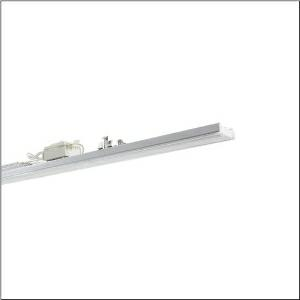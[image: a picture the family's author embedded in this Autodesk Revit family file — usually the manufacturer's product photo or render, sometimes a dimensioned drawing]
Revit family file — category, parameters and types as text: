
# Revit family: licross_11_recessed_mo_51te12dn4axg3s
name_source: partatom
category: Lighting Fixtures
units: mm (PartAtom-declared; Revit-internal decimal feet)

## family parameters
Cut with Voids When Loaded = No
Host = Face
Light Source = No
Part Type = Normal
Room Calculation Point = No
Round Connector Dimension = Use Diameter
Shared = No

## types (1)
- --- (1 x LED, 1010 lm, 6.7 W, 4000K)
    Apparent Load = 7 VA
    CIE Flux Codes = 67 92 99 100 100
    Color Rendering = 80
    Color Temperature = 4000K
    Default Elevation = 1800 mm
    Description = Licross 11 Recessed MO, luminaire insert, of sheet steel, galvanised, coil coated, white, length: 1.500mm, width: 66mm, height: 67mm, LED rated luminous flux: 10.240lm, light colour: 840, SDCM (Standard Deviation of Colour Matching)MacAdam ≤ 2 SDCM (initial), control gear: DALI 2 (for two DALI lines), with plug, 6-pole, with phase selection, for trunking rail, 14-core, mains connection: 220..240V, AC, 50/60Hz, rated input power: 61W, for trunking rail, 14-core, internal wiring halogen-free, for emergency light function, converter,control gear: single battery element, battery: LiFePO4, 9Ah, primary optical cover: cover, of PMMA, light emission: direct distribution, primary light characteristic: symmetric, protection rating (complete): IP54, insulation class (complete): insulation class I (protective earthing), certification: CE, UKCA, protection symbol: D if used in an environment with non-conductive dust loads with corresponding accessories, impact resistance: IK06, permissible ambient temperature for indoor applications: +5..+35°C, standard: EN 60598-2-22, LABS conformity tested according to VDMA 24364:2018-05, reducing of maximum allowable ambient temperature of 5°C with ceiling mounting, corresponds to IFS (International Featured Standards) requirements for safety and quality in the food industry, The light source and the operating device comply with the requirements of the Ecodesign Regulation (EU) 2019/2020 and are replaceable in accordance with this regulation, packaging unit: 1 piece
    Height = 58 mm
    Lamp = 1 x LED
    Lamp Light Flux = 1010 lm
    Lamp Power = 6.7 W
    Lamp count = 1
    Length = 1500 mm
    Luminous efficacy = 151 lm/W
    Manufacturer = Siteco
    ModVariant = No
    Model = 51TE12DN4AXG3S
    Mounting Place = Ceiling
    Mounting Type = Pendant
    Number of Poles = 1
    OnlyDefault = Yes
    Power Factor = 1
    Product Name = Licross 11 Recessed MO
    Product group = luminaire insert | ceiling pendant
    ProductGroupID = 901
    Protection Class = Protection class I
    Protection Degree = IP 54
    RLX_Detail_Level = 1
    RLX_Emergency_Light_Flux = 0 lm
    RLX_Emergency_Type = 0
    RLX_Emergency_Type_DB = No
    RlxData = <blob elided: 25105 chars, md5=cd6c27c4>
    Socket = socket
    Standby Power = 0 W
    System Light Flux = 1010 lm
    System Power = 7 W
    Type Comments = : emergency light operation: 3 h
    Type Image = l_1296930.jpg
    URL = http://relux.com
    VarID = @adj_094191
    Voltage = 0 V
    Weight = 0.00 kg
    Width = 66 mm

## geometry (parser evidence)
native form markers: Blend x4, Sweep x13
no freeform markers — native parametric forms only
